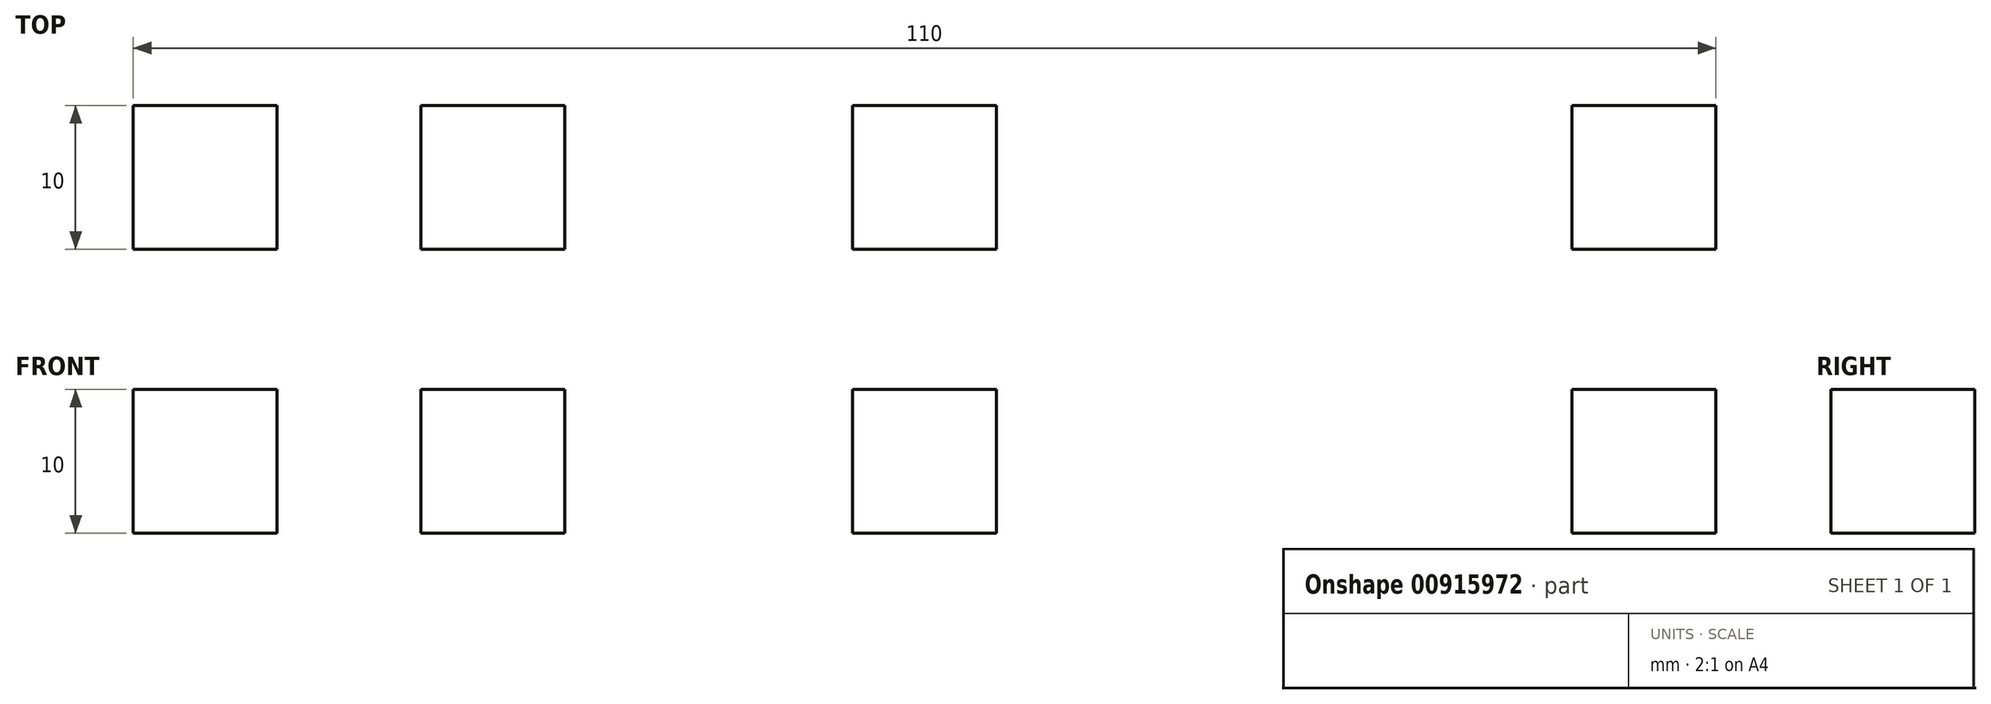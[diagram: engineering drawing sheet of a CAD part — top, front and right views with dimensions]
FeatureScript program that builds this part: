
annotation { "Feature Type Name" : "Feature", "Feature Type Description" : "" }
export const myFeature = defineFeature(function(context is Context, id is Id, definition is map)
    precondition{}
    {
        {
            var Q0;
            Q0=qCreatedBy(makeId("Top.planeOp"),FACE);
            var sketch = newSketch(context, id + "F0", { "sketchPlane" : qUnion([Q0])});
            skLineSegment(sketch, "E0.bottom", {"start": v(-55, 5) * mm, "end": v(-45, 5) * mm});
            skLineSegment(sketch, "E0.top", {"start": v(-55, -5) * mm, "end": v(-45, -5) * mm});
            skLineSegment(sketch, "E0.left", {"start": v(-55, 5) * mm, "end": v(-55, -5) * mm});
            skLineSegment(sketch, "E0.right", {"start": v(-45, 5) * mm, "end": v(-45, -5) * mm});
            skLineSegment(sketch, "E1.bottom", {"start": v(-35, 5) * mm, "end": v(-25, 5) * mm});
            skLineSegment(sketch, "E1.top", {"start": v(-35, -5) * mm, "end": v(-25, -5) * mm});
            skLineSegment(sketch, "E1.left", {"start": v(-35, 5) * mm, "end": v(-35, -5) * mm});
            skLineSegment(sketch, "E1.right", {"start": v(-25, 5) * mm, "end": v(-25, -5) * mm});
            skLineSegment(sketch, "E2.bottom", {"start": v(-5, 5) * mm, "end": v(5, 5) * mm});
            skLineSegment(sketch, "E2.top", {"start": v(-5, -5) * mm, "end": v(5, -5) * mm});
            skLineSegment(sketch, "E2.left", {"start": v(-5, 5) * mm, "end": v(-5, -5) * mm});
            skLineSegment(sketch, "E2.right", {"start": v(5, 5) * mm, "end": v(5, -5) * mm});
            skLineSegment(sketch, "E3.bottom", {"start": v(45, 5) * mm, "end": v(55, 5) * mm});
            skLineSegment(sketch, "E3.top", {"start": v(45, -5) * mm, "end": v(55, -5) * mm});
            skLineSegment(sketch, "E3.left", {"start": v(45, 5) * mm, "end": v(45, -5) * mm});
            skLineSegment(sketch, "E3.right", {"start": v(55, 5) * mm, "end": v(55, -5) * mm});
            skLineSegment(sketch, "E4", {"start": v(-55, 5) * mm, "end": v(55, -5) * mm, "construction": true});
            skSolve(sketch);
        }
        {
            var Q0;
            Q0 = qSketchRegion(id + "F0", true);
            extrude(context, id + "F1", {"entities" : qUnion([Q0]), "depth" : 10 * mm, "offsetDistance" : 25 * mm});
        }
    });
